# Revit family: 1
name_source: partatom
category: Plumbing Fixtures
revit_build: Autodesk Revit 2017 (Build: 20190508_0315(x64)
units: mm (PartAtom-declared; Revit-internal decimal feet)

## family parameters
Always vertical = Yes
Cut with Voids When Loaded = No
OmniClass Number = 23.45.05.14.17
OmniClass Title = Showers
Part Type = Normal
Room Calculation Point = No
Round Connector Dimension = Use Diameter
Shared = Yes
Work Plane-Based = No

## types (3) — shared parameters
AccessibilityPerformance = See ProductInformation for technical PDF
AssetType = Fixed
Category = Pr_40_20_87_76: Shower head holders
CodePerformance = EN 1112, EN 248, EN 1111
Collection = Rondo
Constituents = Shower head holder
DrainSize = 0 mm
DurationUnit = Year
Features = See ProductInformation for technical PDF
HasTray = No
IfcExportAs = IfcSanitaryTerminalType
IfcExportType = Shower
ManufacturerURL = www.noken.com
Material = Brass
NBSDescription = Shower heads
NBSReference = 45-35-70/333
NettWeight = 0.5
NominalDepth = 55 mm  [stored 0.180446 ft]
NominalHeight = 55 mm  [stored 0.180446 ft]
NominalLength = 400 mm  [stored 1.31234 ft]
NominalWidth = 55 mm  [stored 0.180446 ft]
ProductInformation = http://calidad.info-grupo.com:8081
Reference = -
ShowerType = UNSET
Size = 400x55x55
Status = UNSET
SustainabilityPerformance = See ProductInformation for technical PDF
TechnicalDrawing = See ProductInformation for technical PDF
URL = www.noken.com
Uniclass2015Code = Pr_40_20_87_77
Uniclass2015Title = Shower head holders
Uniclass2015Version = V1_9
Version = 1
WarrantyDescription = See ProductInformation for technical PDF
WarrantyDurationUnit = Year
zero-valued in all types: MaterialThickness

## per-type parameters (varying)
| type | BIMObjectName | Color | Finish | MaterialMetal | Model | ModelNumber | ModelReference | Name | ShowerHeadDescription |
| Chrome-100039088 | PGR_Noken_ShowerHeads_Rondo_Chrome-400x55x55mm-100039088 | Chrome | Chrome | PGR_Noken_Brass_Chrome | 100039088 | 100039088 | BRAZO ROCIADOR RONDO 40CM CROMO | ShowerHeads_Rondo_Chrome-400x55x55mm-100039088 | Shower head holder. Material brass, finsih chrome plated, dimension 400x55 , net pdocut weit 0,5 kg. 5 years warranty for superficial finishes and 2 years for the rest of components. EN 1111, EN 1112, EN 248 |
| Black-1002132148 | PGR_Noken_ShowerHeads_Rondo_Black-400x55x55mm-100213248 | Black | Black | PGR_Noken_Brass_Black | 100213248 | 100213248 | BRAZO ROCIADOR RONDO 40CM NEGRO | ShowerHeads_Rondo_Black-400x55x55mm-100213248 | Shower head holder. Material brass, finsih black matt, dimension 400x55 , net pdocut weit 0,5 kg. 5 years warranty for superficial finishes and 2 years for the rest of components. EN 1111, EN 1112, EN 248 |
| White-100253667 | PGR_Noken_ShowerHeads_Rondo_Chrome-400x55x55mm-100039088 | Chrome | Chrome | PGR_Noken_Brass_White | 100253667 | 100039088 | BRAZO ROCIADOR RONDO 40CM CROMO | ShowerHeads_Rondo_Chrome-400x55x55mm-100039088 | Shower head holder. Material brass, finsih chrome plated, dimension 400x55 , net pdocut weit 0,5 kg. 5 years warranty for superficial finishes and 2 years for the rest of components. EN 1111, EN 1112, EN 248 |

note: [stored X ft] marks values corroborated as IEEE doubles in the binary element streams (Revit-internal decimal feet)

## geometry (parser evidence)
native form markers: Blend x2, Sweep x3
no freeform markers — native parametric forms only
